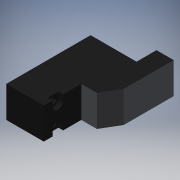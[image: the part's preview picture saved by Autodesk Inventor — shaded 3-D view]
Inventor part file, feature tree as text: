
AUTODESK INVENTOR PART (.ipt)
format: ipt  version: 2018 (Build 220112000, 112)  size: 193,024 bytes
history: native  units: mm
features: extrude x2, hole x2, mirror x1, sketch x1
ambient origin geometry x8: Origin, YZ Plane, XZ Plane, XY Plane, X Axis, Y Axis, Z Axis, Center Point
bodies: Volumenkörper1 (feature_tree)
feature tree (6):
  extrude  "Extrusion1"  Depth=14.7mm
  hole  "Bohrung1"  [1 undecoded]
  extrude  "Extrusion2"  Depth=27.0mm
  mirror  "Spiegeln1"
  hole  "Bohrung2"  [1 undecoded]
  sketch  "Skizze2"  dims[d0=5.5mm d1=14.7mm d3=12.0mm d4=27.0mm d5=12.0mm d6=5.0mm d7=6.4mm d8=16.0mm d9=10.0mm d10=0.0mm d11=1.75mm d12=4.5mm d13=2.0mm d14=6.0mm d15=3.4mm d16=1.5mm d17=90.0deg d18=8.0mm d19=20.594885mm d20=10.0mm d21=0.0mm d22=2.5mm d23=2.5mm d24=2.8mm d25=7.8mm d26=5.0mm d27=5.3mm d28=1.5mm d29=6.0mm d30=4.0mm d31=2.0mm d32=90.0deg d33=8.0mm d34=20.594885mm d35=0.8mm]
note: 2 required parameter values undecoded (feature->parameter linkage not recoverable at this tier; creation-order binding heuristic only, values carry confidence <= 0.55)
